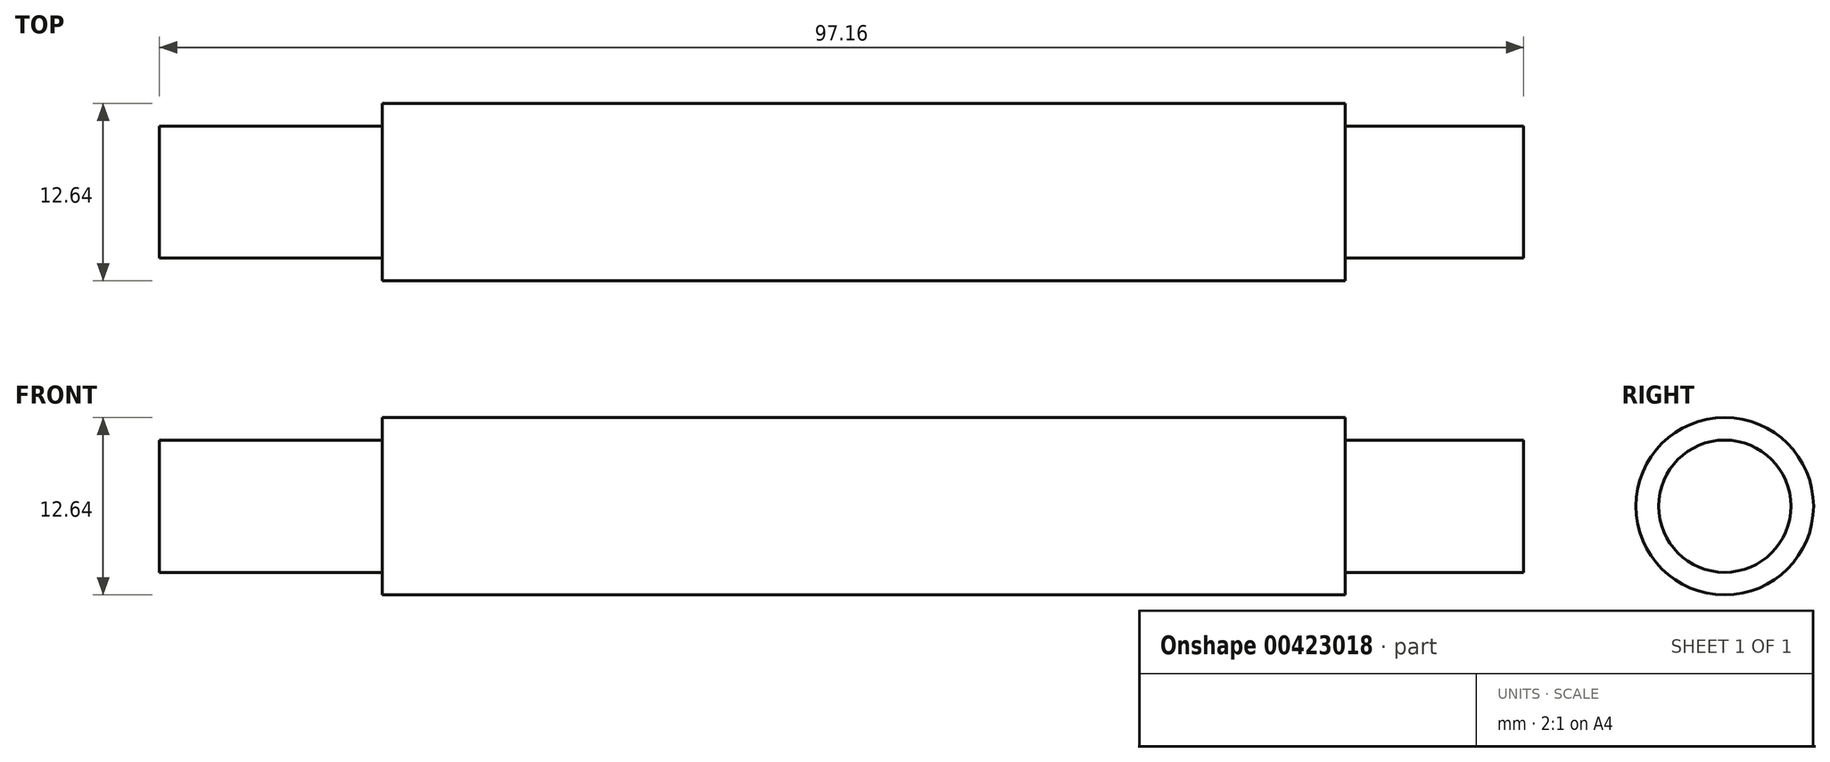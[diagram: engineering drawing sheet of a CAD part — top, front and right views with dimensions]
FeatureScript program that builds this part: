
annotation { "Feature Type Name" : "Feature", "Feature Type Description" : "" }
export const myFeature = defineFeature(function(context is Context, id is Id, definition is map)
    precondition{}
    {
        {
            var Q0;
            Q0=qCreatedBy(makeId("Right.planeOp"),FACE);
            var sketch = newSketch(context, id + "F0", { "sketchPlane" : qUnion([Q0])});
            skCircle(sketch, "E0", {"center": v(0, 0) * mm, "radius": 6.32 * mm});
            skSolve(sketch);
        }
        {
            var Q0;
            Q0=qSketchRegion(id+"F0",true);
            extrude(context, id + "F1", {"entities" : qUnion([Q0]), "depth" : 68.58 * mm});
        }
        {
            var Q0;
            Q0=makeQuery(id+"F1.opExtrude","CAP_FACE",FACE,{"disambiguationData":[OSD([sQuery(id+"F0.wireOp",EDGE,"E0")])],"isStart":false});
            var sketch = newSketch(context, id + "F2", { "sketchPlane" : qUnion([Q0])});
            skCircle(sketch, "E1", {"center": v(0, 0) * mm, "radius": 4.71 * mm});
            skSolve(sketch);
        }
        {
            var Q0;
            Q0=makeQuery(id+"F2.imprint","IMPRINT",FACE,{"disambiguationData":[TD([[makeQuery(id+"F2.imprint","IMPRINT",EDGE,{"derivedFrom":sQuery(id+"F2.wireOp",EDGE,"E1")}),1.0]])]});
            extrude(context, id + "F3", {"entities" : qUnion([Q0]), "operationType" : NewBodyOperationType.ADD, "depth" : 12.7 * mm});
        }
        {
            var Q0;
            Q0=makeQuery(id+"F1.opExtrude","CAP_FACE",FACE,{"disambiguationData":[OSD([sQuery(id+"F0.wireOp",EDGE,"E0")])],"isStart":true});
            var sketch = newSketch(context, id + "F4", { "sketchPlane" : qUnion([Q0])});
            skCircle(sketch, "E2", {"center": v(0, 0) * mm, "radius": 4.71 * mm});
            skSolve(sketch);
        }
        {
            var Q0;
            Q0=makeQuery(id+"F4.imprint","IMPRINT",FACE,{"disambiguationData":[TD([[makeQuery(id+"F4.imprint","IMPRINT",EDGE,{"derivedFrom":sQuery(id+"F4.wireOp",EDGE,"E2")}),1.0]])]});
            extrude(context, id + "F5", {"entities" : qUnion([Q0]), "operationType" : NewBodyOperationType.ADD, "depth" : 15.88 * mm});
        }
    });
